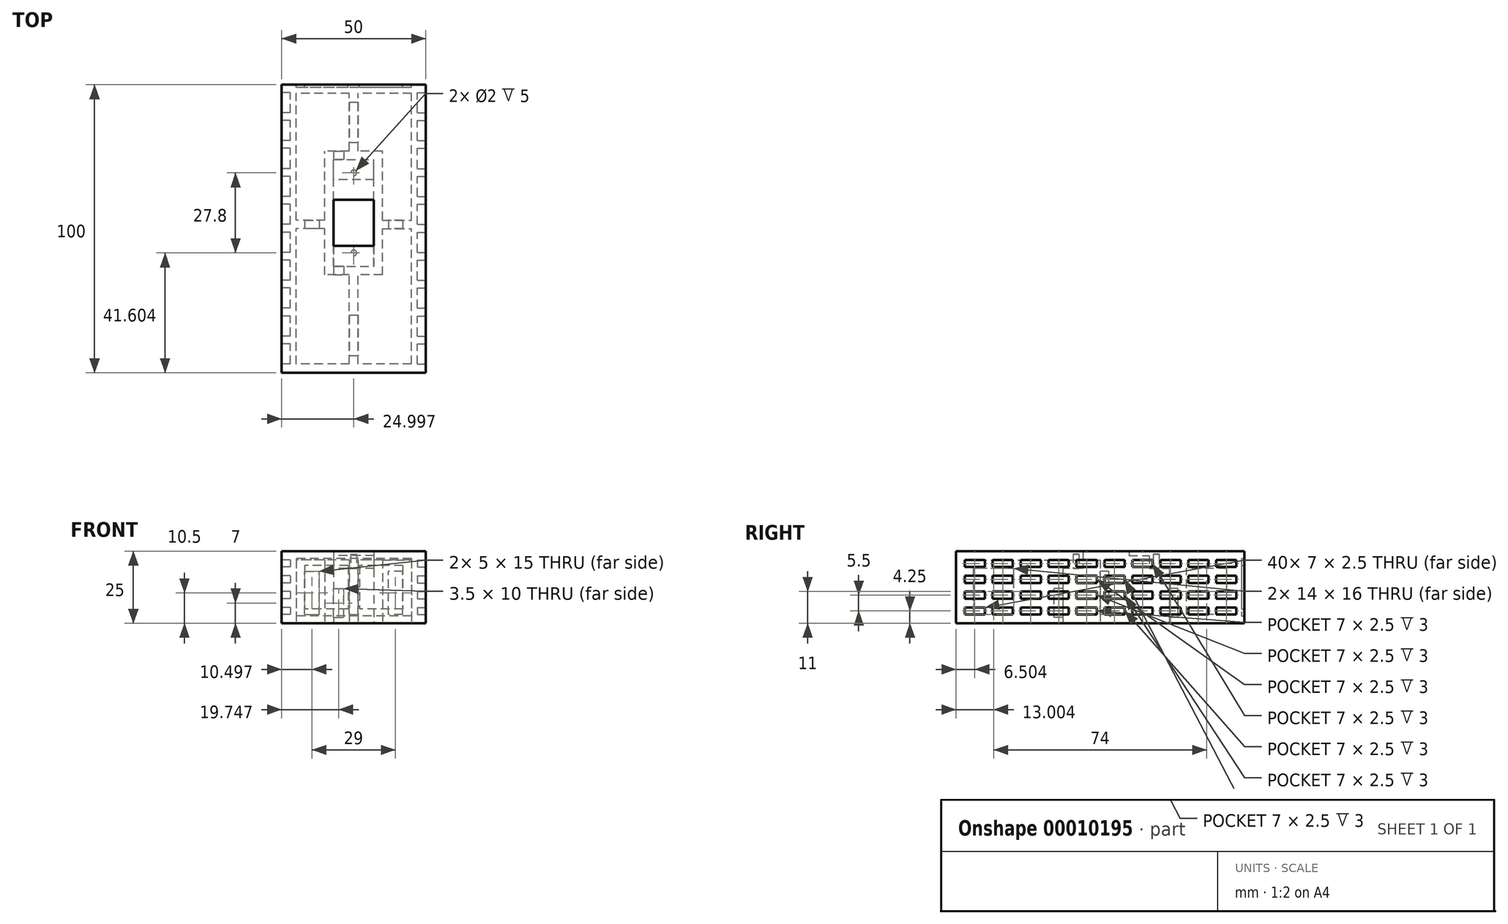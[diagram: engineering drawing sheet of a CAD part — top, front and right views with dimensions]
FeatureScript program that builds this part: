
annotation { "Feature Type Name" : "Feature", "Feature Type Description" : "" }
export const myFeature = defineFeature(function(context is Context, id is Id, definition is map)
    precondition{}
    {
        {
            var Q0;
            Q0=qCreatedBy(makeId("Top.planeOp"),FACE);
            var sketch = newSketch(context, id + "F0", { "sketchPlane" : qUnion([Q0])});
            skLineSegment(sketch, "E0.bottom", {"start": v(-33.78, -32.6) * mm, "end": v(16.22, -32.6) * mm});
            skLineSegment(sketch, "E0.top", {"start": v(-33.78, 67.4) * mm, "end": v(16.22, 67.4) * mm});
            skLineSegment(sketch, "E0.left", {"start": v(-33.78, -32.6) * mm, "end": v(-33.78, 67.4) * mm});
            skLineSegment(sketch, "E0.right", {"start": v(16.22, -32.6) * mm, "end": v(16.22, 67.4) * mm});
            skSolve(sketch);
        }
        {
            var Q0;
            Q0 = qSketchRegion(id + "F0", true);
            extrude(context, id + "F1", {"entities" : qUnion([Q0]), "depth" : 25 * mm});
        }
        {
            var Q0;
            Q0=makeQuery(id+"F1.opExtrude","CAP_FACE",FACE,{"disambiguationData":[OSD([sQuery(id+"F0.wireOp",EDGE,"E0.bottom"),sQuery(id+"F0.wireOp",EDGE,"E0.top"),sQuery(id+"F0.wireOp",EDGE,"E0.left"),sQuery(id+"F0.wireOp",EDGE,"E0.right")])],"isStart":true});
            var sketch = newSketch(context, id + "F2", { "sketchPlane" : qUnion([Q0])});
            skLineSegment(sketch, "E1.bottom", {"start": v(-1.78, -11.4) * mm, "end": v(-15.78, -11.4) * mm});
            skLineSegment(sketch, "E1.top", {"start": v(-1.78, -34.4) * mm, "end": v(-15.78, -34.4) * mm});
            skLineSegment(sketch, "E1.left", {"start": v(-1.78, -11.4) * mm, "end": v(-1.78, -34.4) * mm});
            skLineSegment(sketch, "E1.right", {"start": v(-15.78, -11.4) * mm, "end": v(-15.78, -34.4) * mm});
            skSolve(sketch);
        }
        {
            var Q0;
            Q0 = qSketchRegion(id + "F2", true);
            extrude(context, id + "F3", {"entities" : qUnion([Q0]), "operationType" : NewBodyOperationType.REMOVE, "oppositeDirection" : true, "depth" : 23.5 * mm});
        }
        {
            var Q0;
            Q0=makeQuery(id+"F1.opExtrude","CAP_FACE",FACE,{"disambiguationData":[OSD([sQuery(id+"F0.wireOp",EDGE,"E0.bottom"),sQuery(id+"F0.wireOp",EDGE,"E0.top"),sQuery(id+"F0.wireOp",EDGE,"E0.left"),sQuery(id+"F0.wireOp",EDGE,"E0.right")])],"isStart":true});
            var sketch = newSketch(context, id + "F4", { "sketchPlane" : qUnion([Q0])});
            skLineSegment(sketch, "E2.bottom", {"start": v(-15.78, -11.4) * mm, "end": v(-1.78, -11.4) * mm});
            skLineSegment(sketch, "E2.top", {"start": v(-15.78, -4.4) * mm, "end": v(-1.78, -4.4) * mm});
            skLineSegment(sketch, "E2.left", {"start": v(-15.78, -11.4) * mm, "end": v(-15.78, -4.4) * mm});
            skLineSegment(sketch, "E2.right", {"start": v(-1.78, -11.4) * mm, "end": v(-1.78, -4.4) * mm});
            skLineSegment(sketch, "E3.bottom", {"start": v(-15.78, -34.4) * mm, "end": v(-1.78, -34.4) * mm});
            skLineSegment(sketch, "E3.top", {"start": v(-15.78, -41.4) * mm, "end": v(-1.78, -41.4) * mm});
            skLineSegment(sketch, "E3.left", {"start": v(-15.78, -34.4) * mm, "end": v(-15.78, -41.4) * mm});
            skLineSegment(sketch, "E3.right", {"start": v(-1.78, -34.4) * mm, "end": v(-1.78, -41.4) * mm});
            skSolve(sketch);
        }
        {
            var Q0;
            Q0 = qSketchRegion(id + "F4", true);
            extrude(context, id + "F5", {"entities" : qUnion([Q0]), "operationType" : NewBodyOperationType.REMOVE, "oppositeDirection" : true, "depth" : 19 * mm});
        }
        {
            var Q0;
            Q0=makeQuery(id+"F3.boolean.opBoolean","COPY",FACE,{"derivedFrom":makeQuery(id+"F3.opExtrude","CAP_FACE",FACE,{"disambiguationData":[OSD([sQuery(id+"F2.wireOp",EDGE,"E1.bottom"),sQuery(id+"F2.wireOp",EDGE,"E1.top"),sQuery(id+"F2.wireOp",EDGE,"E1.left"),sQuery(id+"F2.wireOp",EDGE,"E1.right")])],"isStart":false})});
            var sketch = newSketch(context, id + "F6", { "sketchPlane" : qUnion([Q0])});
            skLineSegment(sketch, "E4.bottom", {"start": v(-15.78, -11.4) * mm, "end": v(-1.78, -11.4) * mm});
            skLineSegment(sketch, "E4.top", {"start": v(-15.78, -27.4) * mm, "end": v(-1.78, -27.4) * mm});
            skLineSegment(sketch, "E4.left", {"start": v(-15.78, -11.4) * mm, "end": v(-15.78, -27.4) * mm});
            skLineSegment(sketch, "E4.right", {"start": v(-1.78, -11.4) * mm, "end": v(-1.78, -27.4) * mm});
            skSolve(sketch);
        }
        {
            var Q0;
            Q0 = qSketchRegion(id + "F6", true);
            extrude(context, id + "F7", {"entities" : qUnion([Q0]), "operationType" : NewBodyOperationType.REMOVE, "endBound" : BoundingType.UP_TO_NEXT, "oppositeDirection" : true, "depth" : 25 * mm});
        }
        {
            var Q0;
            Q0=makeQuery(id+"F5.boolean.opBoolean","COPY",FACE,{"derivedFrom":makeQuery(id+"F5.opExtrude","CAP_FACE",FACE,{"disambiguationData":[OSD([sQuery(id+"F4.wireOp",EDGE,"E2.bottom"),sQuery(id+"F4.wireOp",EDGE,"E2.top"),sQuery(id+"F4.wireOp",EDGE,"E2.left"),sQuery(id+"F4.wireOp",EDGE,"E2.right")])],"isStart":false})});
            var sketch = newSketch(context, id + "F8", { "sketchPlane" : qUnion([Q0])});
            skCircle(sketch, "E5", {"center": v(-8.78, -9) * mm, "radius": 1 * mm});
            skCircle(sketch, "E6", {"center": v(-8.78, -36.8) * mm, "radius": 1 * mm});
            skSolve(sketch);
        }
        {
            var Q0;
            Q0 = qSketchRegion(id + "F8", true);
            extrude(context, id + "F9", {"entities" : qUnion([Q0]), "operationType" : NewBodyOperationType.REMOVE, "oppositeDirection" : true, "depth" : 5 * mm});
        }
        {
            var Q0;
            Q0=makeQuery(id+"F1.opExtrude","SWEPT_FACE",FACE,{"disambiguationData":[OSD([sQuery(id+"F0.wireOp",EDGE,"E0.right")])]});
            var sketch = newSketch(context, id + "F10", { "sketchPlane" : qUnion([Q0])});
            skLineSegment(sketch, "E7.bottom", {"start": v(-29.6, 22) * mm, "end": v(-22.6, 22) * mm});
            skLineSegment(sketch, "E7.top", {"start": v(-29.6, 19.5) * mm, "end": v(-22.6, 19.5) * mm});
            skLineSegment(sketch, "E7.left", {"start": v(-29.6, 22) * mm, "end": v(-29.6, 19.5) * mm});
            skLineSegment(sketch, "E7.right", {"start": v(-22.6, 22) * mm, "end": v(-22.6, 19.5) * mm});
            skLineSegment(sketch, "E8.0.1.0", {"start": v(-29.6, 14) * mm, "end": v(-22.6, 14) * mm});
            skLineSegment(sketch, "E8.0.1.1", {"start": v(-22.6, 16.5) * mm, "end": v(-22.6, 14) * mm});
            skLineSegment(sketch, "E8.0.1.2", {"start": v(-29.6, 16.5) * mm, "end": v(-22.6, 16.5) * mm});
            skLineSegment(sketch, "E8.0.1.3", {"start": v(-29.6, 16.5) * mm, "end": v(-29.6, 14) * mm});
            skLineSegment(sketch, "E8.0.2.0", {"start": v(-29.6, 8.5) * mm, "end": v(-22.6, 8.5) * mm});
            skLineSegment(sketch, "E8.0.2.1", {"start": v(-22.6, 11) * mm, "end": v(-22.6, 8.5) * mm});
            skLineSegment(sketch, "E8.0.2.2", {"start": v(-29.6, 11) * mm, "end": v(-22.6, 11) * mm});
            skLineSegment(sketch, "E8.0.2.3", {"start": v(-29.6, 11) * mm, "end": v(-29.6, 8.5) * mm});
            skLineSegment(sketch, "E8.0.3.0", {"start": v(-29.6, 3) * mm, "end": v(-22.6, 3) * mm});
            skLineSegment(sketch, "E8.0.3.1", {"start": v(-22.6, 5.5) * mm, "end": v(-22.6, 3) * mm});
            skLineSegment(sketch, "E8.0.3.2", {"start": v(-29.6, 5.5) * mm, "end": v(-22.6, 5.5) * mm});
            skLineSegment(sketch, "E8.0.3.3", {"start": v(-29.6, 5.5) * mm, "end": v(-29.6, 3) * mm});
            skLineSegment(sketch, "E8.1.0.0", {"start": v(-19.9, 19.5) * mm, "end": v(-12.9, 19.5) * mm});
            skLineSegment(sketch, "E8.1.0.1", {"start": v(-12.9, 22) * mm, "end": v(-12.9, 19.5) * mm});
            skLineSegment(sketch, "E8.1.0.2", {"start": v(-19.9, 22) * mm, "end": v(-12.9, 22) * mm});
            skLineSegment(sketch, "E8.1.0.3", {"start": v(-19.9, 22) * mm, "end": v(-19.9, 19.5) * mm});
            skLineSegment(sketch, "E8.1.1.0", {"start": v(-19.9, 14) * mm, "end": v(-12.9, 14) * mm});
            skLineSegment(sketch, "E8.1.1.1", {"start": v(-12.9, 16.5) * mm, "end": v(-12.9, 14) * mm});
            skLineSegment(sketch, "E8.1.1.2", {"start": v(-19.9, 16.5) * mm, "end": v(-12.9, 16.5) * mm});
            skLineSegment(sketch, "E8.1.1.3", {"start": v(-19.9, 16.5) * mm, "end": v(-19.9, 14) * mm});
            skLineSegment(sketch, "E8.1.2.0", {"start": v(-19.9, 8.5) * mm, "end": v(-12.9, 8.5) * mm});
            skLineSegment(sketch, "E8.1.2.1", {"start": v(-12.9, 11) * mm, "end": v(-12.9, 8.5) * mm});
            skLineSegment(sketch, "E8.1.2.2", {"start": v(-19.9, 11) * mm, "end": v(-12.9, 11) * mm});
            skLineSegment(sketch, "E8.1.2.3", {"start": v(-19.9, 11) * mm, "end": v(-19.9, 8.5) * mm});
            skLineSegment(sketch, "E8.1.3.0", {"start": v(-19.9, 3) * mm, "end": v(-12.9, 3) * mm});
            skLineSegment(sketch, "E8.1.3.1", {"start": v(-12.9, 5.5) * mm, "end": v(-12.9, 3) * mm});
            skLineSegment(sketch, "E8.1.3.2", {"start": v(-19.9, 5.5) * mm, "end": v(-12.9, 5.5) * mm});
            skLineSegment(sketch, "E8.1.3.3", {"start": v(-19.9, 5.5) * mm, "end": v(-19.9, 3) * mm});
            skLineSegment(sketch, "E8.2.0.0", {"start": v(-10.2, 19.5) * mm, "end": v(-3.2, 19.5) * mm});
            skLineSegment(sketch, "E8.2.0.1", {"start": v(-3.2, 22) * mm, "end": v(-3.2, 19.5) * mm});
            skLineSegment(sketch, "E8.2.0.2", {"start": v(-10.2, 22) * mm, "end": v(-3.2, 22) * mm});
            skLineSegment(sketch, "E8.2.0.3", {"start": v(-10.2, 22) * mm, "end": v(-10.2, 19.5) * mm});
            skLineSegment(sketch, "E8.2.1.0", {"start": v(-10.2, 14) * mm, "end": v(-3.2, 14) * mm});
            skLineSegment(sketch, "E8.2.1.1", {"start": v(-3.2, 16.5) * mm, "end": v(-3.2, 14) * mm});
            skLineSegment(sketch, "E8.2.1.2", {"start": v(-10.2, 16.5) * mm, "end": v(-3.2, 16.5) * mm});
            skLineSegment(sketch, "E8.2.1.3", {"start": v(-10.2, 16.5) * mm, "end": v(-10.2, 14) * mm});
            skLineSegment(sketch, "E8.2.2.0", {"start": v(-10.2, 8.5) * mm, "end": v(-3.2, 8.5) * mm});
            skLineSegment(sketch, "E8.2.2.1", {"start": v(-3.2, 11) * mm, "end": v(-3.2, 8.5) * mm});
            skLineSegment(sketch, "E8.2.2.2", {"start": v(-10.2, 11) * mm, "end": v(-3.2, 11) * mm});
            skLineSegment(sketch, "E8.2.2.3", {"start": v(-10.2, 11) * mm, "end": v(-10.2, 8.5) * mm});
            skLineSegment(sketch, "E8.2.3.0", {"start": v(-10.2, 3) * mm, "end": v(-3.2, 3) * mm});
            skLineSegment(sketch, "E8.2.3.1", {"start": v(-3.2, 5.5) * mm, "end": v(-3.2, 3) * mm});
            skLineSegment(sketch, "E8.2.3.2", {"start": v(-10.2, 5.5) * mm, "end": v(-3.2, 5.5) * mm});
            skLineSegment(sketch, "E8.2.3.3", {"start": v(-10.2, 5.5) * mm, "end": v(-10.2, 3) * mm});
            skLineSegment(sketch, "E8.3.0.0", {"start": v(-0.5, 19.5) * mm, "end": v(6.5, 19.5) * mm});
            skLineSegment(sketch, "E8.3.0.1", {"start": v(6.5, 22) * mm, "end": v(6.5, 19.5) * mm});
            skLineSegment(sketch, "E8.3.0.2", {"start": v(-0.5, 22) * mm, "end": v(6.5, 22) * mm});
            skLineSegment(sketch, "E8.3.0.3", {"start": v(-0.5, 22) * mm, "end": v(-0.5, 19.5) * mm});
            skLineSegment(sketch, "E8.3.1.0", {"start": v(-0.5, 14) * mm, "end": v(6.5, 14) * mm});
            skLineSegment(sketch, "E8.3.1.1", {"start": v(6.5, 16.5) * mm, "end": v(6.5, 14) * mm});
            skLineSegment(sketch, "E8.3.1.2", {"start": v(-0.5, 16.5) * mm, "end": v(6.5, 16.5) * mm});
            skLineSegment(sketch, "E8.3.1.3", {"start": v(-0.5, 16.5) * mm, "end": v(-0.5, 14) * mm});
            skLineSegment(sketch, "E8.3.2.0", {"start": v(-0.5, 8.5) * mm, "end": v(6.5, 8.5) * mm});
            skLineSegment(sketch, "E8.3.2.1", {"start": v(6.5, 11) * mm, "end": v(6.5, 8.5) * mm});
            skLineSegment(sketch, "E8.3.2.2", {"start": v(-0.5, 11) * mm, "end": v(6.5, 11) * mm});
            skLineSegment(sketch, "E8.3.2.3", {"start": v(-0.5, 11) * mm, "end": v(-0.5, 8.5) * mm});
            skLineSegment(sketch, "E8.3.3.0", {"start": v(-0.5, 3) * mm, "end": v(6.5, 3) * mm});
            skLineSegment(sketch, "E8.3.3.1", {"start": v(6.5, 5.5) * mm, "end": v(6.5, 3) * mm});
            skLineSegment(sketch, "E8.3.3.2", {"start": v(-0.5, 5.5) * mm, "end": v(6.5, 5.5) * mm});
            skLineSegment(sketch, "E8.3.3.3", {"start": v(-0.5, 5.5) * mm, "end": v(-0.5, 3) * mm});
            skLineSegment(sketch, "E8.4.0.0", {"start": v(9.2, 19.5) * mm, "end": v(16.2, 19.5) * mm});
            skLineSegment(sketch, "E8.4.0.1", {"start": v(16.2, 22) * mm, "end": v(16.2, 19.5) * mm});
            skLineSegment(sketch, "E8.4.0.2", {"start": v(9.2, 22) * mm, "end": v(16.2, 22) * mm});
            skLineSegment(sketch, "E8.4.0.3", {"start": v(9.2, 22) * mm, "end": v(9.2, 19.5) * mm});
            skLineSegment(sketch, "E8.4.1.0", {"start": v(9.2, 14) * mm, "end": v(16.2, 14) * mm});
            skLineSegment(sketch, "E8.4.1.1", {"start": v(16.2, 16.5) * mm, "end": v(16.2, 14) * mm});
            skLineSegment(sketch, "E8.4.1.2", {"start": v(9.2, 16.5) * mm, "end": v(16.2, 16.5) * mm});
            skLineSegment(sketch, "E8.4.1.3", {"start": v(9.2, 16.5) * mm, "end": v(9.2, 14) * mm});
            skLineSegment(sketch, "E8.4.2.0", {"start": v(9.2, 8.5) * mm, "end": v(16.2, 8.5) * mm});
            skLineSegment(sketch, "E8.4.2.1", {"start": v(16.2, 11) * mm, "end": v(16.2, 8.5) * mm});
            skLineSegment(sketch, "E8.4.2.2", {"start": v(9.2, 11) * mm, "end": v(16.2, 11) * mm});
            skLineSegment(sketch, "E8.4.2.3", {"start": v(9.2, 11) * mm, "end": v(9.2, 8.5) * mm});
            skLineSegment(sketch, "E8.4.3.0", {"start": v(9.2, 3) * mm, "end": v(16.2, 3) * mm});
            skLineSegment(sketch, "E8.4.3.1", {"start": v(16.2, 5.5) * mm, "end": v(16.2, 3) * mm});
            skLineSegment(sketch, "E8.4.3.2", {"start": v(9.2, 5.5) * mm, "end": v(16.2, 5.5) * mm});
            skLineSegment(sketch, "E8.4.3.3", {"start": v(9.2, 5.5) * mm, "end": v(9.2, 3) * mm});
            skLineSegment(sketch, "E8.5.0.0", {"start": v(18.9, 19.5) * mm, "end": v(25.9, 19.5) * mm});
            skLineSegment(sketch, "E8.5.0.1", {"start": v(25.9, 22) * mm, "end": v(25.9, 19.5) * mm});
            skLineSegment(sketch, "E8.5.0.2", {"start": v(18.9, 22) * mm, "end": v(25.9, 22) * mm});
            skLineSegment(sketch, "E8.5.0.3", {"start": v(18.9, 22) * mm, "end": v(18.9, 19.5) * mm});
            skLineSegment(sketch, "E8.5.1.0", {"start": v(18.9, 14) * mm, "end": v(25.9, 14) * mm});
            skLineSegment(sketch, "E8.5.1.1", {"start": v(25.9, 16.5) * mm, "end": v(25.9, 14) * mm});
            skLineSegment(sketch, "E8.5.1.2", {"start": v(18.9, 16.5) * mm, "end": v(25.9, 16.5) * mm});
            skLineSegment(sketch, "E8.5.1.3", {"start": v(18.9, 16.5) * mm, "end": v(18.9, 14) * mm});
            skLineSegment(sketch, "E8.5.2.0", {"start": v(18.9, 8.5) * mm, "end": v(25.9, 8.5) * mm});
            skLineSegment(sketch, "E8.5.2.1", {"start": v(25.9, 11) * mm, "end": v(25.9, 8.5) * mm});
            skLineSegment(sketch, "E8.5.2.2", {"start": v(18.9, 11) * mm, "end": v(25.9, 11) * mm});
            skLineSegment(sketch, "E8.5.2.3", {"start": v(18.9, 11) * mm, "end": v(18.9, 8.5) * mm});
            skLineSegment(sketch, "E8.5.3.0", {"start": v(18.9, 3) * mm, "end": v(25.9, 3) * mm});
            skLineSegment(sketch, "E8.5.3.1", {"start": v(25.9, 5.5) * mm, "end": v(25.9, 3) * mm});
            skLineSegment(sketch, "E8.5.3.2", {"start": v(18.9, 5.5) * mm, "end": v(25.9, 5.5) * mm});
            skLineSegment(sketch, "E8.5.3.3", {"start": v(18.9, 5.5) * mm, "end": v(18.9, 3) * mm});
            skLineSegment(sketch, "E8.6.0.0", {"start": v(28.6, 19.5) * mm, "end": v(35.6, 19.5) * mm});
            skLineSegment(sketch, "E8.6.0.1", {"start": v(35.6, 22) * mm, "end": v(35.6, 19.5) * mm});
            skLineSegment(sketch, "E8.6.0.2", {"start": v(28.6, 22) * mm, "end": v(35.6, 22) * mm});
            skLineSegment(sketch, "E8.6.0.3", {"start": v(28.6, 22) * mm, "end": v(28.6, 19.5) * mm});
            skLineSegment(sketch, "E8.6.1.0", {"start": v(28.6, 14) * mm, "end": v(35.6, 14) * mm});
            skLineSegment(sketch, "E8.6.1.1", {"start": v(35.6, 16.5) * mm, "end": v(35.6, 14) * mm});
            skLineSegment(sketch, "E8.6.1.2", {"start": v(28.6, 16.5) * mm, "end": v(35.6, 16.5) * mm});
            skLineSegment(sketch, "E8.6.1.3", {"start": v(28.6, 16.5) * mm, "end": v(28.6, 14) * mm});
            skLineSegment(sketch, "E8.6.2.0", {"start": v(28.6, 8.5) * mm, "end": v(35.6, 8.5) * mm});
            skLineSegment(sketch, "E8.6.2.1", {"start": v(35.6, 11) * mm, "end": v(35.6, 8.5) * mm});
            skLineSegment(sketch, "E8.6.2.2", {"start": v(28.6, 11) * mm, "end": v(35.6, 11) * mm});
            skLineSegment(sketch, "E8.6.2.3", {"start": v(28.6, 11) * mm, "end": v(28.6, 8.5) * mm});
            skLineSegment(sketch, "E8.6.3.0", {"start": v(28.6, 3) * mm, "end": v(35.6, 3) * mm});
            skLineSegment(sketch, "E8.6.3.1", {"start": v(35.6, 5.5) * mm, "end": v(35.6, 3) * mm});
            skLineSegment(sketch, "E8.6.3.2", {"start": v(28.6, 5.5) * mm, "end": v(35.6, 5.5) * mm});
            skLineSegment(sketch, "E8.6.3.3", {"start": v(28.6, 5.5) * mm, "end": v(28.6, 3) * mm});
            skLineSegment(sketch, "E8.7.0.0", {"start": v(38.3, 19.5) * mm, "end": v(45.3, 19.5) * mm});
            skLineSegment(sketch, "E8.7.0.1", {"start": v(45.3, 22) * mm, "end": v(45.3, 19.5) * mm});
            skLineSegment(sketch, "E8.7.0.2", {"start": v(38.3, 22) * mm, "end": v(45.3, 22) * mm});
            skLineSegment(sketch, "E8.7.0.3", {"start": v(38.3, 22) * mm, "end": v(38.3, 19.5) * mm});
            skLineSegment(sketch, "E8.7.1.0", {"start": v(38.3, 14) * mm, "end": v(45.3, 14) * mm});
            skLineSegment(sketch, "E8.7.1.1", {"start": v(45.3, 16.5) * mm, "end": v(45.3, 14) * mm});
            skLineSegment(sketch, "E8.7.1.2", {"start": v(38.3, 16.5) * mm, "end": v(45.3, 16.5) * mm});
            skLineSegment(sketch, "E8.7.1.3", {"start": v(38.3, 16.5) * mm, "end": v(38.3, 14) * mm});
            skLineSegment(sketch, "E8.7.2.0", {"start": v(38.3, 8.5) * mm, "end": v(45.3, 8.5) * mm});
            skLineSegment(sketch, "E8.7.2.1", {"start": v(45.3, 11) * mm, "end": v(45.3, 8.5) * mm});
            skLineSegment(sketch, "E8.7.2.2", {"start": v(38.3, 11) * mm, "end": v(45.3, 11) * mm});
            skLineSegment(sketch, "E8.7.2.3", {"start": v(38.3, 11) * mm, "end": v(38.3, 8.5) * mm});
            skLineSegment(sketch, "E8.7.3.0", {"start": v(38.3, 3) * mm, "end": v(45.3, 3) * mm});
            skLineSegment(sketch, "E8.7.3.1", {"start": v(45.3, 5.5) * mm, "end": v(45.3, 3) * mm});
            skLineSegment(sketch, "E8.7.3.2", {"start": v(38.3, 5.5) * mm, "end": v(45.3, 5.5) * mm});
            skLineSegment(sketch, "E8.7.3.3", {"start": v(38.3, 5.5) * mm, "end": v(38.3, 3) * mm});
            skLineSegment(sketch, "E8.8.0.0", {"start": v(48, 19.5) * mm, "end": v(55, 19.5) * mm});
            skLineSegment(sketch, "E8.8.0.1", {"start": v(55, 22) * mm, "end": v(55, 19.5) * mm});
            skLineSegment(sketch, "E8.8.0.2", {"start": v(48, 22) * mm, "end": v(55, 22) * mm});
            skLineSegment(sketch, "E8.8.0.3", {"start": v(48, 22) * mm, "end": v(48, 19.5) * mm});
            skLineSegment(sketch, "E8.8.1.0", {"start": v(48, 14) * mm, "end": v(55, 14) * mm});
            skLineSegment(sketch, "E8.8.1.1", {"start": v(55, 16.5) * mm, "end": v(55, 14) * mm});
            skLineSegment(sketch, "E8.8.1.2", {"start": v(48, 16.5) * mm, "end": v(55, 16.5) * mm});
            skLineSegment(sketch, "E8.8.1.3", {"start": v(48, 16.5) * mm, "end": v(48, 14) * mm});
            skLineSegment(sketch, "E8.8.2.0", {"start": v(48, 8.5) * mm, "end": v(55, 8.5) * mm});
            skLineSegment(sketch, "E8.8.2.1", {"start": v(55, 11) * mm, "end": v(55, 8.5) * mm});
            skLineSegment(sketch, "E8.8.2.2", {"start": v(48, 11) * mm, "end": v(55, 11) * mm});
            skLineSegment(sketch, "E8.8.2.3", {"start": v(48, 11) * mm, "end": v(48, 8.5) * mm});
            skLineSegment(sketch, "E8.8.3.0", {"start": v(48, 3) * mm, "end": v(55, 3) * mm});
            skLineSegment(sketch, "E8.8.3.1", {"start": v(55, 5.5) * mm, "end": v(55, 3) * mm});
            skLineSegment(sketch, "E8.8.3.2", {"start": v(48, 5.5) * mm, "end": v(55, 5.5) * mm});
            skLineSegment(sketch, "E8.8.3.3", {"start": v(48, 5.5) * mm, "end": v(48, 3) * mm});
            skLineSegment(sketch, "E8.9.0.0", {"start": v(57.7, 19.5) * mm, "end": v(64.7, 19.5) * mm});
            skLineSegment(sketch, "E8.9.0.1", {"start": v(64.7, 22) * mm, "end": v(64.7, 19.5) * mm});
            skLineSegment(sketch, "E8.9.0.2", {"start": v(57.7, 22) * mm, "end": v(64.7, 22) * mm});
            skLineSegment(sketch, "E8.9.0.3", {"start": v(57.7, 22) * mm, "end": v(57.7, 19.5) * mm});
            skLineSegment(sketch, "E8.9.1.0", {"start": v(57.7, 14) * mm, "end": v(64.7, 14) * mm});
            skLineSegment(sketch, "E8.9.1.1", {"start": v(64.7, 16.5) * mm, "end": v(64.7, 14) * mm});
            skLineSegment(sketch, "E8.9.1.2", {"start": v(57.7, 16.5) * mm, "end": v(64.7, 16.5) * mm});
            skLineSegment(sketch, "E8.9.1.3", {"start": v(57.7, 16.5) * mm, "end": v(57.7, 14) * mm});
            skLineSegment(sketch, "E8.9.2.0", {"start": v(57.7, 8.5) * mm, "end": v(64.7, 8.5) * mm});
            skLineSegment(sketch, "E8.9.2.1", {"start": v(64.7, 11) * mm, "end": v(64.7, 8.5) * mm});
            skLineSegment(sketch, "E8.9.2.2", {"start": v(57.7, 11) * mm, "end": v(64.7, 11) * mm});
            skLineSegment(sketch, "E8.9.2.3", {"start": v(57.7, 11) * mm, "end": v(57.7, 8.5) * mm});
            skLineSegment(sketch, "E8.9.3.0", {"start": v(57.7, 3) * mm, "end": v(64.7, 3) * mm});
            skLineSegment(sketch, "E8.9.3.1", {"start": v(64.7, 5.5) * mm, "end": v(64.7, 3) * mm});
            skLineSegment(sketch, "E8.9.3.2", {"start": v(57.7, 5.5) * mm, "end": v(64.7, 5.5) * mm});
            skLineSegment(sketch, "E8.9.3.3", {"start": v(57.7, 5.5) * mm, "end": v(57.7, 3) * mm});
            skLineSegment(sketch, "E8.direction1", {"start": v(-29.6, 19.5) * mm, "end": v(-19.9, 19.5) * mm, "construction": true});
            skLineSegment(sketch, "E8.direction2", {"start": v(-29.6, 19.5) * mm, "end": v(-29.6, 14) * mm, "construction": true});
            skSolve(sketch);
        }
        {
            var Q0;
            Q0 = qSketchRegion(id + "F10", true);
            extrude(context, id + "F11", {"entities" : qUnion([Q0]), "operationType" : NewBodyOperationType.REMOVE, "oppositeDirection" : true, "depth" : 3 * mm});
        }
        {
            var Q0;
            Q0=makeQuery(id+"F1.opExtrude","SWEPT_FACE",FACE,{"disambiguationData":[OSD([sQuery(id+"F0.wireOp",EDGE,"E0.left")])]});
            var sketch = newSketch(context, id + "F12", { "sketchPlane" : qUnion([Q0])});
            skLineSegment(sketch, "E9.bottom", {"start": v(29.6, 22) * mm, "end": v(22.6, 22) * mm});
            skLineSegment(sketch, "E9.top", {"start": v(29.6, 19.5) * mm, "end": v(22.6, 19.5) * mm});
            skLineSegment(sketch, "E9.left", {"start": v(29.6, 22) * mm, "end": v(29.6, 19.5) * mm});
            skLineSegment(sketch, "E9.right", {"start": v(22.6, 22) * mm, "end": v(22.6, 19.5) * mm});
            skLineSegment(sketch, "E10.0.1.0", {"start": v(29.6, 14) * mm, "end": v(22.6, 14) * mm});
            skLineSegment(sketch, "E10.0.1.1", {"start": v(29.6, 16.5) * mm, "end": v(29.6, 14) * mm});
            skLineSegment(sketch, "E10.0.1.2", {"start": v(29.6, 16.5) * mm, "end": v(22.6, 16.5) * mm});
            skLineSegment(sketch, "E10.0.1.3", {"start": v(22.6, 16.5) * mm, "end": v(22.6, 14) * mm});
            skLineSegment(sketch, "E10.0.2.0", {"start": v(29.6, 8.5) * mm, "end": v(22.6, 8.5) * mm});
            skLineSegment(sketch, "E10.0.2.1", {"start": v(29.6, 11) * mm, "end": v(29.6, 8.5) * mm});
            skLineSegment(sketch, "E10.0.2.2", {"start": v(29.6, 11) * mm, "end": v(22.6, 11) * mm});
            skLineSegment(sketch, "E10.0.2.3", {"start": v(22.6, 11) * mm, "end": v(22.6, 8.5) * mm});
            skLineSegment(sketch, "E10.0.3.0", {"start": v(29.6, 3) * mm, "end": v(22.6, 3) * mm});
            skLineSegment(sketch, "E10.0.3.1", {"start": v(29.6, 5.5) * mm, "end": v(29.6, 3) * mm});
            skLineSegment(sketch, "E10.0.3.2", {"start": v(29.6, 5.5) * mm, "end": v(22.6, 5.5) * mm});
            skLineSegment(sketch, "E10.0.3.3", {"start": v(22.6, 5.5) * mm, "end": v(22.6, 3) * mm});
            skLineSegment(sketch, "E10.1.0.0", {"start": v(19.9, 19.5) * mm, "end": v(12.9, 19.5) * mm});
            skLineSegment(sketch, "E10.1.0.1", {"start": v(19.9, 22) * mm, "end": v(19.9, 19.5) * mm});
            skLineSegment(sketch, "E10.1.0.2", {"start": v(19.9, 22) * mm, "end": v(12.9, 22) * mm});
            skLineSegment(sketch, "E10.1.0.3", {"start": v(12.9, 22) * mm, "end": v(12.9, 19.5) * mm});
            skLineSegment(sketch, "E10.1.1.0", {"start": v(19.9, 14) * mm, "end": v(12.9, 14) * mm});
            skLineSegment(sketch, "E10.1.1.1", {"start": v(19.9, 16.5) * mm, "end": v(19.9, 14) * mm});
            skLineSegment(sketch, "E10.1.1.2", {"start": v(19.9, 16.5) * mm, "end": v(12.9, 16.5) * mm});
            skLineSegment(sketch, "E10.1.1.3", {"start": v(12.9, 16.5) * mm, "end": v(12.9, 14) * mm});
            skLineSegment(sketch, "E10.1.2.0", {"start": v(19.9, 8.5) * mm, "end": v(12.9, 8.5) * mm});
            skLineSegment(sketch, "E10.1.2.1", {"start": v(19.9, 11) * mm, "end": v(19.9, 8.5) * mm});
            skLineSegment(sketch, "E10.1.2.2", {"start": v(19.9, 11) * mm, "end": v(12.9, 11) * mm});
            skLineSegment(sketch, "E10.1.2.3", {"start": v(12.9, 11) * mm, "end": v(12.9, 8.5) * mm});
            skLineSegment(sketch, "E10.1.3.0", {"start": v(19.9, 3) * mm, "end": v(12.9, 3) * mm});
            skLineSegment(sketch, "E10.1.3.1", {"start": v(19.9, 5.5) * mm, "end": v(19.9, 3) * mm});
            skLineSegment(sketch, "E10.1.3.2", {"start": v(19.9, 5.5) * mm, "end": v(12.9, 5.5) * mm});
            skLineSegment(sketch, "E10.1.3.3", {"start": v(12.9, 5.5) * mm, "end": v(12.9, 3) * mm});
            skLineSegment(sketch, "E10.2.0.0", {"start": v(10.2, 19.5) * mm, "end": v(3.2, 19.5) * mm});
            skLineSegment(sketch, "E10.2.0.1", {"start": v(10.2, 22) * mm, "end": v(10.2, 19.5) * mm});
            skLineSegment(sketch, "E10.2.0.2", {"start": v(10.2, 22) * mm, "end": v(3.2, 22) * mm});
            skLineSegment(sketch, "E10.2.0.3", {"start": v(3.2, 22) * mm, "end": v(3.2, 19.5) * mm});
            skLineSegment(sketch, "E10.2.1.0", {"start": v(10.2, 14) * mm, "end": v(3.2, 14) * mm});
            skLineSegment(sketch, "E10.2.1.1", {"start": v(10.2, 16.5) * mm, "end": v(10.2, 14) * mm});
            skLineSegment(sketch, "E10.2.1.2", {"start": v(10.2, 16.5) * mm, "end": v(3.2, 16.5) * mm});
            skLineSegment(sketch, "E10.2.1.3", {"start": v(3.2, 16.5) * mm, "end": v(3.2, 14) * mm});
            skLineSegment(sketch, "E10.2.2.0", {"start": v(10.2, 8.5) * mm, "end": v(3.2, 8.5) * mm});
            skLineSegment(sketch, "E10.2.2.1", {"start": v(10.2, 11) * mm, "end": v(10.2, 8.5) * mm});
            skLineSegment(sketch, "E10.2.2.2", {"start": v(10.2, 11) * mm, "end": v(3.2, 11) * mm});
            skLineSegment(sketch, "E10.2.2.3", {"start": v(3.2, 11) * mm, "end": v(3.2, 8.5) * mm});
            skLineSegment(sketch, "E10.2.3.0", {"start": v(10.2, 3) * mm, "end": v(3.2, 3) * mm});
            skLineSegment(sketch, "E10.2.3.1", {"start": v(10.2, 5.5) * mm, "end": v(10.2, 3) * mm});
            skLineSegment(sketch, "E10.2.3.2", {"start": v(10.2, 5.5) * mm, "end": v(3.2, 5.5) * mm});
            skLineSegment(sketch, "E10.2.3.3", {"start": v(3.2, 5.5) * mm, "end": v(3.2, 3) * mm});
            skLineSegment(sketch, "E10.3.0.0", {"start": v(0.5, 19.5) * mm, "end": v(-6.5, 19.5) * mm});
            skLineSegment(sketch, "E10.3.0.1", {"start": v(0.5, 22) * mm, "end": v(0.5, 19.5) * mm});
            skLineSegment(sketch, "E10.3.0.2", {"start": v(0.5, 22) * mm, "end": v(-6.5, 22) * mm});
            skLineSegment(sketch, "E10.3.0.3", {"start": v(-6.5, 22) * mm, "end": v(-6.5, 19.5) * mm});
            skLineSegment(sketch, "E10.3.1.0", {"start": v(0.5, 14) * mm, "end": v(-6.5, 14) * mm});
            skLineSegment(sketch, "E10.3.1.1", {"start": v(0.5, 16.5) * mm, "end": v(0.5, 14) * mm});
            skLineSegment(sketch, "E10.3.1.2", {"start": v(0.5, 16.5) * mm, "end": v(-6.5, 16.5) * mm});
            skLineSegment(sketch, "E10.3.1.3", {"start": v(-6.5, 16.5) * mm, "end": v(-6.5, 14) * mm});
            skLineSegment(sketch, "E10.3.2.0", {"start": v(0.5, 8.5) * mm, "end": v(-6.5, 8.5) * mm});
            skLineSegment(sketch, "E10.3.2.1", {"start": v(0.5, 11) * mm, "end": v(0.5, 8.5) * mm});
            skLineSegment(sketch, "E10.3.2.2", {"start": v(0.5, 11) * mm, "end": v(-6.5, 11) * mm});
            skLineSegment(sketch, "E10.3.2.3", {"start": v(-6.5, 11) * mm, "end": v(-6.5, 8.5) * mm});
            skLineSegment(sketch, "E10.3.3.0", {"start": v(0.5, 3) * mm, "end": v(-6.5, 3) * mm});
            skLineSegment(sketch, "E10.3.3.1", {"start": v(0.5, 5.5) * mm, "end": v(0.5, 3) * mm});
            skLineSegment(sketch, "E10.3.3.2", {"start": v(0.5, 5.5) * mm, "end": v(-6.5, 5.5) * mm});
            skLineSegment(sketch, "E10.3.3.3", {"start": v(-6.5, 5.5) * mm, "end": v(-6.5, 3) * mm});
            skLineSegment(sketch, "E10.4.0.0", {"start": v(-9.2, 19.5) * mm, "end": v(-16.2, 19.5) * mm});
            skLineSegment(sketch, "E10.4.0.1", {"start": v(-9.2, 22) * mm, "end": v(-9.2, 19.5) * mm});
            skLineSegment(sketch, "E10.4.0.2", {"start": v(-9.2, 22) * mm, "end": v(-16.2, 22) * mm});
            skLineSegment(sketch, "E10.4.0.3", {"start": v(-16.2, 22) * mm, "end": v(-16.2, 19.5) * mm});
            skLineSegment(sketch, "E10.4.1.0", {"start": v(-9.2, 14) * mm, "end": v(-16.2, 14) * mm});
            skLineSegment(sketch, "E10.4.1.1", {"start": v(-9.2, 16.5) * mm, "end": v(-9.2, 14) * mm});
            skLineSegment(sketch, "E10.4.1.2", {"start": v(-9.2, 16.5) * mm, "end": v(-16.2, 16.5) * mm});
            skLineSegment(sketch, "E10.4.1.3", {"start": v(-16.2, 16.5) * mm, "end": v(-16.2, 14) * mm});
            skLineSegment(sketch, "E10.4.2.0", {"start": v(-9.2, 8.5) * mm, "end": v(-16.2, 8.5) * mm});
            skLineSegment(sketch, "E10.4.2.1", {"start": v(-9.2, 11) * mm, "end": v(-9.2, 8.5) * mm});
            skLineSegment(sketch, "E10.4.2.2", {"start": v(-9.2, 11) * mm, "end": v(-16.2, 11) * mm});
            skLineSegment(sketch, "E10.4.2.3", {"start": v(-16.2, 11) * mm, "end": v(-16.2, 8.5) * mm});
            skLineSegment(sketch, "E10.4.3.0", {"start": v(-9.2, 3) * mm, "end": v(-16.2, 3) * mm});
            skLineSegment(sketch, "E10.4.3.1", {"start": v(-9.2, 5.5) * mm, "end": v(-9.2, 3) * mm});
            skLineSegment(sketch, "E10.4.3.2", {"start": v(-9.2, 5.5) * mm, "end": v(-16.2, 5.5) * mm});
            skLineSegment(sketch, "E10.4.3.3", {"start": v(-16.2, 5.5) * mm, "end": v(-16.2, 3) * mm});
            skLineSegment(sketch, "E10.5.0.0", {"start": v(-18.9, 19.5) * mm, "end": v(-25.9, 19.5) * mm});
            skLineSegment(sketch, "E10.5.0.1", {"start": v(-18.9, 22) * mm, "end": v(-18.9, 19.5) * mm});
            skLineSegment(sketch, "E10.5.0.2", {"start": v(-18.9, 22) * mm, "end": v(-25.9, 22) * mm});
            skLineSegment(sketch, "E10.5.0.3", {"start": v(-25.9, 22) * mm, "end": v(-25.9, 19.5) * mm});
            skLineSegment(sketch, "E10.5.1.0", {"start": v(-18.9, 14) * mm, "end": v(-25.9, 14) * mm});
            skLineSegment(sketch, "E10.5.1.1", {"start": v(-18.9, 16.5) * mm, "end": v(-18.9, 14) * mm});
            skLineSegment(sketch, "E10.5.1.2", {"start": v(-18.9, 16.5) * mm, "end": v(-25.9, 16.5) * mm});
            skLineSegment(sketch, "E10.5.1.3", {"start": v(-25.9, 16.5) * mm, "end": v(-25.9, 14) * mm});
            skLineSegment(sketch, "E10.5.2.0", {"start": v(-18.9, 8.5) * mm, "end": v(-25.9, 8.5) * mm});
            skLineSegment(sketch, "E10.5.2.1", {"start": v(-18.9, 11) * mm, "end": v(-18.9, 8.5) * mm});
            skLineSegment(sketch, "E10.5.2.2", {"start": v(-18.9, 11) * mm, "end": v(-25.9, 11) * mm});
            skLineSegment(sketch, "E10.5.2.3", {"start": v(-25.9, 11) * mm, "end": v(-25.9, 8.5) * mm});
            skLineSegment(sketch, "E10.5.3.0", {"start": v(-18.9, 3) * mm, "end": v(-25.9, 3) * mm});
            skLineSegment(sketch, "E10.5.3.1", {"start": v(-18.9, 5.5) * mm, "end": v(-18.9, 3) * mm});
            skLineSegment(sketch, "E10.5.3.2", {"start": v(-18.9, 5.5) * mm, "end": v(-25.9, 5.5) * mm});
            skLineSegment(sketch, "E10.5.3.3", {"start": v(-25.9, 5.5) * mm, "end": v(-25.9, 3) * mm});
            skLineSegment(sketch, "E10.6.0.0", {"start": v(-28.6, 19.5) * mm, "end": v(-35.6, 19.5) * mm});
            skLineSegment(sketch, "E10.6.0.1", {"start": v(-28.6, 22) * mm, "end": v(-28.6, 19.5) * mm});
            skLineSegment(sketch, "E10.6.0.2", {"start": v(-28.6, 22) * mm, "end": v(-35.6, 22) * mm});
            skLineSegment(sketch, "E10.6.0.3", {"start": v(-35.6, 22) * mm, "end": v(-35.6, 19.5) * mm});
            skLineSegment(sketch, "E10.6.1.0", {"start": v(-28.6, 14) * mm, "end": v(-35.6, 14) * mm});
            skLineSegment(sketch, "E10.6.1.1", {"start": v(-28.6, 16.5) * mm, "end": v(-28.6, 14) * mm});
            skLineSegment(sketch, "E10.6.1.2", {"start": v(-28.6, 16.5) * mm, "end": v(-35.6, 16.5) * mm});
            skLineSegment(sketch, "E10.6.1.3", {"start": v(-35.6, 16.5) * mm, "end": v(-35.6, 14) * mm});
            skLineSegment(sketch, "E10.6.2.0", {"start": v(-28.6, 8.5) * mm, "end": v(-35.6, 8.5) * mm});
            skLineSegment(sketch, "E10.6.2.1", {"start": v(-28.6, 11) * mm, "end": v(-28.6, 8.5) * mm});
            skLineSegment(sketch, "E10.6.2.2", {"start": v(-28.6, 11) * mm, "end": v(-35.6, 11) * mm});
            skLineSegment(sketch, "E10.6.2.3", {"start": v(-35.6, 11) * mm, "end": v(-35.6, 8.5) * mm});
            skLineSegment(sketch, "E10.6.3.0", {"start": v(-28.6, 3) * mm, "end": v(-35.6, 3) * mm});
            skLineSegment(sketch, "E10.6.3.1", {"start": v(-28.6, 5.5) * mm, "end": v(-28.6, 3) * mm});
            skLineSegment(sketch, "E10.6.3.2", {"start": v(-28.6, 5.5) * mm, "end": v(-35.6, 5.5) * mm});
            skLineSegment(sketch, "E10.6.3.3", {"start": v(-35.6, 5.5) * mm, "end": v(-35.6, 3) * mm});
            skLineSegment(sketch, "E10.7.0.0", {"start": v(-38.3, 19.5) * mm, "end": v(-45.3, 19.5) * mm});
            skLineSegment(sketch, "E10.7.0.1", {"start": v(-38.3, 22) * mm, "end": v(-38.3, 19.5) * mm});
            skLineSegment(sketch, "E10.7.0.2", {"start": v(-38.3, 22) * mm, "end": v(-45.3, 22) * mm});
            skLineSegment(sketch, "E10.7.0.3", {"start": v(-45.3, 22) * mm, "end": v(-45.3, 19.5) * mm});
            skLineSegment(sketch, "E10.7.1.0", {"start": v(-38.3, 14) * mm, "end": v(-45.3, 14) * mm});
            skLineSegment(sketch, "E10.7.1.1", {"start": v(-38.3, 16.5) * mm, "end": v(-38.3, 14) * mm});
            skLineSegment(sketch, "E10.7.1.2", {"start": v(-38.3, 16.5) * mm, "end": v(-45.3, 16.5) * mm});
            skLineSegment(sketch, "E10.7.1.3", {"start": v(-45.3, 16.5) * mm, "end": v(-45.3, 14) * mm});
            skLineSegment(sketch, "E10.7.2.0", {"start": v(-38.3, 8.5) * mm, "end": v(-45.3, 8.5) * mm});
            skLineSegment(sketch, "E10.7.2.1", {"start": v(-38.3, 11) * mm, "end": v(-38.3, 8.5) * mm});
            skLineSegment(sketch, "E10.7.2.2", {"start": v(-38.3, 11) * mm, "end": v(-45.3, 11) * mm});
            skLineSegment(sketch, "E10.7.2.3", {"start": v(-45.3, 11) * mm, "end": v(-45.3, 8.5) * mm});
            skLineSegment(sketch, "E10.7.3.0", {"start": v(-38.3, 3) * mm, "end": v(-45.3, 3) * mm});
            skLineSegment(sketch, "E10.7.3.1", {"start": v(-38.3, 5.5) * mm, "end": v(-38.3, 3) * mm});
            skLineSegment(sketch, "E10.7.3.2", {"start": v(-38.3, 5.5) * mm, "end": v(-45.3, 5.5) * mm});
            skLineSegment(sketch, "E10.7.3.3", {"start": v(-45.3, 5.5) * mm, "end": v(-45.3, 3) * mm});
            skLineSegment(sketch, "E10.8.0.0", {"start": v(-48, 19.5) * mm, "end": v(-55, 19.5) * mm});
            skLineSegment(sketch, "E10.8.0.1", {"start": v(-48, 22) * mm, "end": v(-48, 19.5) * mm});
            skLineSegment(sketch, "E10.8.0.2", {"start": v(-48, 22) * mm, "end": v(-55, 22) * mm});
            skLineSegment(sketch, "E10.8.0.3", {"start": v(-55, 22) * mm, "end": v(-55, 19.5) * mm});
            skLineSegment(sketch, "E10.8.1.0", {"start": v(-48, 14) * mm, "end": v(-55, 14) * mm});
            skLineSegment(sketch, "E10.8.1.1", {"start": v(-48, 16.5) * mm, "end": v(-48, 14) * mm});
            skLineSegment(sketch, "E10.8.1.2", {"start": v(-48, 16.5) * mm, "end": v(-55, 16.5) * mm});
            skLineSegment(sketch, "E10.8.1.3", {"start": v(-55, 16.5) * mm, "end": v(-55, 14) * mm});
            skLineSegment(sketch, "E10.8.2.0", {"start": v(-48, 8.5) * mm, "end": v(-55, 8.5) * mm});
            skLineSegment(sketch, "E10.8.2.1", {"start": v(-48, 11) * mm, "end": v(-48, 8.5) * mm});
            skLineSegment(sketch, "E10.8.2.2", {"start": v(-48, 11) * mm, "end": v(-55, 11) * mm});
            skLineSegment(sketch, "E10.8.2.3", {"start": v(-55, 11) * mm, "end": v(-55, 8.5) * mm});
            skLineSegment(sketch, "E10.8.3.0", {"start": v(-48, 3) * mm, "end": v(-55, 3) * mm});
            skLineSegment(sketch, "E10.8.3.1", {"start": v(-48, 5.5) * mm, "end": v(-48, 3) * mm});
            skLineSegment(sketch, "E10.8.3.2", {"start": v(-48, 5.5) * mm, "end": v(-55, 5.5) * mm});
            skLineSegment(sketch, "E10.8.3.3", {"start": v(-55, 5.5) * mm, "end": v(-55, 3) * mm});
            skLineSegment(sketch, "E10.9.0.0", {"start": v(-57.7, 19.5) * mm, "end": v(-64.7, 19.5) * mm});
            skLineSegment(sketch, "E10.9.0.1", {"start": v(-57.7, 22) * mm, "end": v(-57.7, 19.5) * mm});
            skLineSegment(sketch, "E10.9.0.2", {"start": v(-57.7, 22) * mm, "end": v(-64.7, 22) * mm});
            skLineSegment(sketch, "E10.9.0.3", {"start": v(-64.7, 22) * mm, "end": v(-64.7, 19.5) * mm});
            skLineSegment(sketch, "E10.9.1.0", {"start": v(-57.7, 14) * mm, "end": v(-64.7, 14) * mm});
            skLineSegment(sketch, "E10.9.1.1", {"start": v(-57.7, 16.5) * mm, "end": v(-57.7, 14) * mm});
            skLineSegment(sketch, "E10.9.1.2", {"start": v(-57.7, 16.5) * mm, "end": v(-64.7, 16.5) * mm});
            skLineSegment(sketch, "E10.9.1.3", {"start": v(-64.7, 16.5) * mm, "end": v(-64.7, 14) * mm});
            skLineSegment(sketch, "E10.9.2.0", {"start": v(-57.7, 8.5) * mm, "end": v(-64.7, 8.5) * mm});
            skLineSegment(sketch, "E10.9.2.1", {"start": v(-57.7, 11) * mm, "end": v(-57.7, 8.5) * mm});
            skLineSegment(sketch, "E10.9.2.2", {"start": v(-57.7, 11) * mm, "end": v(-64.7, 11) * mm});
            skLineSegment(sketch, "E10.9.2.3", {"start": v(-64.7, 11) * mm, "end": v(-64.7, 8.5) * mm});
            skLineSegment(sketch, "E10.9.3.0", {"start": v(-57.7, 3) * mm, "end": v(-64.7, 3) * mm});
            skLineSegment(sketch, "E10.9.3.1", {"start": v(-57.7, 5.5) * mm, "end": v(-57.7, 3) * mm});
            skLineSegment(sketch, "E10.9.3.2", {"start": v(-57.7, 5.5) * mm, "end": v(-64.7, 5.5) * mm});
            skLineSegment(sketch, "E10.9.3.3", {"start": v(-64.7, 5.5) * mm, "end": v(-64.7, 3) * mm});
            skLineSegment(sketch, "E10.direction1", {"start": v(22.6, 19.5) * mm, "end": v(12.9, 19.5) * mm, "construction": true});
            skLineSegment(sketch, "E10.direction2", {"start": v(22.6, 19.5) * mm, "end": v(22.6, 14) * mm, "construction": true});
            skSolve(sketch);
        }
        {
            var Q0;
            Q0 = qSketchRegion(id + "F12", true);
            extrude(context, id + "F13", {"entities" : qUnion([Q0]), "operationType" : NewBodyOperationType.REMOVE, "oppositeDirection" : true, "depth" : 3 * mm});
        }
        {
            var Q0;
            Q0=makeQuery(id+"F1.opExtrude","SWEPT_FACE",FACE,{"disambiguationData":[OSD([sQuery(id+"F0.wireOp",EDGE,"E0.top")])]});
            var sketch = newSketch(context, id + "F14", { "sketchPlane" : qUnion([Q0])});
            skLineSegment(sketch, "E11.bottom", {"start": v(-11.22, 22.5) * mm, "end": v(28.78, 22.5) * mm});
            skLineSegment(sketch, "E11.top", {"start": v(-11.22, 2.5) * mm, "end": v(28.78, 2.5) * mm});
            skLineSegment(sketch, "E11.left", {"start": v(-11.22, 22.5) * mm, "end": v(-11.22, 2.5) * mm});
            skLineSegment(sketch, "E11.right", {"start": v(28.78, 22.5) * mm, "end": v(28.78, 2.5) * mm});
            skLineSegment(sketch, "E12.bottom", {"start": v(10.78, 20) * mm, "end": v(25.78, 20) * mm});
            skLineSegment(sketch, "E12.top", {"start": v(10.78, 5) * mm, "end": v(25.78, 5) * mm});
            skLineSegment(sketch, "E12.left", {"start": v(10.78, 20) * mm, "end": v(10.78, 5) * mm});
            skLineSegment(sketch, "E12.right", {"start": v(25.78, 20) * mm, "end": v(25.78, 5) * mm});
            skLineSegment(sketch, "E13.bottom", {"start": v(-8.22, 20) * mm, "end": v(6.78, 20) * mm});
            skLineSegment(sketch, "E13.top", {"start": v(-8.22, 5) * mm, "end": v(6.78, 5) * mm});
            skLineSegment(sketch, "E13.left", {"start": v(-8.22, 20) * mm, "end": v(-8.22, 5) * mm});
            skLineSegment(sketch, "E13.right", {"start": v(6.78, 20) * mm, "end": v(6.78, 5) * mm});
            skSolve(sketch);
        }
        {
            var Q0;
            Q0 = qSketchRegion(id + "F14", true);
            extrude(context, id + "F15", {"entities" : qUnion([Q0]), "operationType" : NewBodyOperationType.REMOVE, "oppositeDirection" : true, "depth" : 1 * mm});
        }
        {
            var Q0;
            Q0=makeQuery(id+"F1.opExtrude","CAP_FACE",FACE,{"disambiguationData":[OSD([sQuery(id+"F0.wireOp",EDGE,"E0.bottom"),sQuery(id+"F0.wireOp",EDGE,"E0.top"),sQuery(id+"F0.wireOp",EDGE,"E0.left"),sQuery(id+"F0.wireOp",EDGE,"E0.right")])],"isStart":true});
            var sketch = newSketch(context, id + "F16", { "sketchPlane" : qUnion([Q0])});
            skLineSegment(sketch, "E14.bottom", {"start": v(11.22, 29.6) * mm, "end": v(-7.28, 29.6) * mm});
            skLineSegment(sketch, "E14.top", {"start": v(11.22, -64.4) * mm, "end": v(-7.28, -64.4) * mm});
            skLineSegment(sketch, "E14.left", {"start": v(11.22, 29.6) * mm, "end": v(11.22, -17.4) * mm});
            skLineSegment(sketch, "E14.right", {"start": v(-28.78, 29.6) * mm, "end": v(-28.78, -17.4) * mm});
            skLineSegment(sketch, "E15.bottom", {"start": v(1.22, -1.4) * mm, "end": v(-7.28, -1.4) * mm});
            skLineSegment(sketch, "E15.top", {"start": v(1.22, -44.4) * mm, "end": v(-7.28, -44.4) * mm});
            skLineSegment(sketch, "E15.left", {"start": v(1.22, -1.4) * mm, "end": v(1.22, -17.4) * mm});
            skLineSegment(sketch, "E15.right", {"start": v(-18.78, -1.4) * mm, "end": v(-18.78, -17.4) * mm});
            skLineSegment(sketch, "E16.bottom", {"start": v(1.22, -20.4) * mm, "end": v(11.22, -20.4) * mm});
            skLineSegment(sketch, "E16.top", {"start": v(1.22, -17.4) * mm, "end": v(11.22, -17.4) * mm});
            skLineSegment(sketch, "E17.bottom", {"start": v(-18.78, -17.4) * mm, "end": v(-28.78, -17.4) * mm});
            skLineSegment(sketch, "E17.top", {"start": v(-18.78, -20.4) * mm, "end": v(-28.78, -20.4) * mm});
            skLineSegment(sketch, "E18.left", {"start": v(-7.28, 29.6) * mm, "end": v(-7.28, -1.4) * mm});
            skLineSegment(sketch, "E18.right", {"start": v(-10.28, 29.6) * mm, "end": v(-10.28, -1.4) * mm});
            skLineSegment(sketch, "E19.left", {"start": v(-10.28, -44.4) * mm, "end": v(-10.28, -64.4) * mm});
            skLineSegment(sketch, "E19.right", {"start": v(-7.28, -44.4) * mm, "end": v(-7.28, -64.4) * mm});
            skLineSegment(sketch, "E20.trimOffspring", {"start": v(-10.28, -1.4) * mm, "end": v(-18.78, -1.4) * mm});
            skLineSegment(sketch, "E21.trimOffspring", {"start": v(1.22, -20.4) * mm, "end": v(1.22, -44.4) * mm});
            skLineSegment(sketch, "E22.trimOffspring", {"start": v(11.22, -20.4) * mm, "end": v(11.22, -64.4) * mm});
            skLineSegment(sketch, "E23.trimOffspring", {"start": v(-28.78, -20.4) * mm, "end": v(-28.78, -64.4) * mm});
            skLineSegment(sketch, "E24.trimOffspring", {"start": v(-18.78, -20.4) * mm, "end": v(-18.78, -44.4) * mm});
            skLineSegment(sketch, "E25.trimOffspring", {"start": v(-10.28, -44.4) * mm, "end": v(-18.78, -44.4) * mm});
            skLineSegment(sketch, "E26.trimOffspring", {"start": v(-10.28, -64.4) * mm, "end": v(-28.78, -64.4) * mm});
            skLineSegment(sketch, "E27.trimOffspring", {"start": v(-10.28, 29.6) * mm, "end": v(-28.78, 29.6) * mm});
            skSolve(sketch);
        }
        {
            var Q0;
            Q0 = qSketchRegion(id + "F16", true);
            extrude(context, id + "F17", {"entities" : qUnion([Q0]), "operationType" : NewBodyOperationType.REMOVE, "oppositeDirection" : true, "depth" : 22 * mm});
        }
        {
            var Q0;
            Q0=makeQuery(id+"F17.boolean.opBoolean","COPY",FACE,{"derivedFrom":makeQuery(id+"F17.opExtrude","SWEPT_FACE",FACE,{"disambiguationData":[OSD([sQuery(id+"F16.wireOp",EDGE,"E20.trimOffspring")])]})});
            var sketch = newSketch(context, id + "F18", { "sketchPlane" : qUnion([Q0])});
            skLineSegment(sketch, "E28.bottom", {"start": v(-15.78, 2) * mm, "end": v(-12.28, 2) * mm});
            skLineSegment(sketch, "E28.top", {"start": v(-15.78, 12) * mm, "end": v(-12.28, 12) * mm});
            skLineSegment(sketch, "E28.left", {"start": v(-15.78, 2) * mm, "end": v(-15.78, 12) * mm});
            skLineSegment(sketch, "E28.right", {"start": v(-12.28, 2) * mm, "end": v(-12.28, 12) * mm});
            skSolve(sketch);
        }
        {
            var Q0;
            Q0 = qSketchRegion(id + "F18", true);
            extrude(context, id + "F19", {"entities" : qUnion([Q0]), "operationType" : NewBodyOperationType.REMOVE, "oppositeDirection" : true, "depth" : 50 * mm});
        }
        {
            var Q0;
            Q0=makeQuery(id+"F17.boolean.opBoolean","COPY",FACE,{"derivedFrom":makeQuery(id+"F17.opExtrude","SWEPT_FACE",FACE,{"disambiguationData":[OSD([sQuery(id+"F16.wireOp",EDGE,"E19.right")])]})});
            var sketch = newSketch(context, id + "F20", { "sketchPlane" : qUnion([Q0])});
            skLineSegment(sketch, "E29.bottom", {"start": v(61.4, 3) * mm, "end": v(47.4, 3) * mm});
            skLineSegment(sketch, "E29.top", {"start": v(61.4, 19) * mm, "end": v(47.4, 19) * mm});
            skLineSegment(sketch, "E29.left", {"start": v(61.4, 3) * mm, "end": v(61.4, 19) * mm});
            skLineSegment(sketch, "E29.right", {"start": v(47.4, 3) * mm, "end": v(47.4, 19) * mm});
            skLineSegment(sketch, "E30.bottom", {"start": v(-12.6, 3) * mm, "end": v(-26.6, 3) * mm});
            skLineSegment(sketch, "E30.top", {"start": v(-12.6, 19) * mm, "end": v(-26.6, 19) * mm});
            skLineSegment(sketch, "E30.left", {"start": v(-12.6, 3) * mm, "end": v(-12.6, 19) * mm});
            skLineSegment(sketch, "E30.right", {"start": v(-26.6, 3) * mm, "end": v(-26.6, 19) * mm});
            skSolve(sketch);
        }
        {
            var Q0;
            Q0 = qSketchRegion(id + "F20", true);
            extrude(context, id + "F21", {"entities" : qUnion([Q0]), "operationType" : NewBodyOperationType.REMOVE, "endBound" : BoundingType.UP_TO_NEXT, "oppositeDirection" : true, "depth" : 25 * mm});
        }
        {
            var Q0;
            Q0=makeQuery(id+"F17.boolean.opBoolean","COPY",FACE,{"derivedFrom":makeQuery(id+"F17.opExtrude","SWEPT_FACE",FACE,{"disambiguationData":[OSD([sQuery(id+"F16.wireOp",EDGE,"E16.top")])]})});
            var sketch = newSketch(context, id + "F22", { "sketchPlane" : qUnion([Q0])});
            skLineSegment(sketch, "E31.bottom", {"start": v(8.22, 3) * mm, "end": v(3.22, 3) * mm});
            skLineSegment(sketch, "E31.top", {"start": v(8.22, 18) * mm, "end": v(3.22, 18) * mm});
            skLineSegment(sketch, "E31.left", {"start": v(8.22, 3) * mm, "end": v(8.22, 18) * mm});
            skLineSegment(sketch, "E31.right", {"start": v(3.22, 3) * mm, "end": v(3.22, 18) * mm});
            skLineSegment(sketch, "E32.bottom", {"start": v(-20.78, 18) * mm, "end": v(-25.78, 18) * mm});
            skLineSegment(sketch, "E32.top", {"start": v(-20.78, 3) * mm, "end": v(-25.78, 3) * mm});
            skLineSegment(sketch, "E32.left", {"start": v(-20.78, 18) * mm, "end": v(-20.78, 3) * mm});
            skLineSegment(sketch, "E32.right", {"start": v(-25.78, 18) * mm, "end": v(-25.78, 3) * mm});
            skSolve(sketch);
        }
        {
            var Q0;
            Q0 = qSketchRegion(id + "F22", true);
            extrude(context, id + "F23", {"entities" : qUnion([Q0]), "operationType" : NewBodyOperationType.REMOVE, "endBound" : BoundingType.UP_TO_NEXT, "oppositeDirection" : true, "depth" : 25 * mm});
        }
    });
